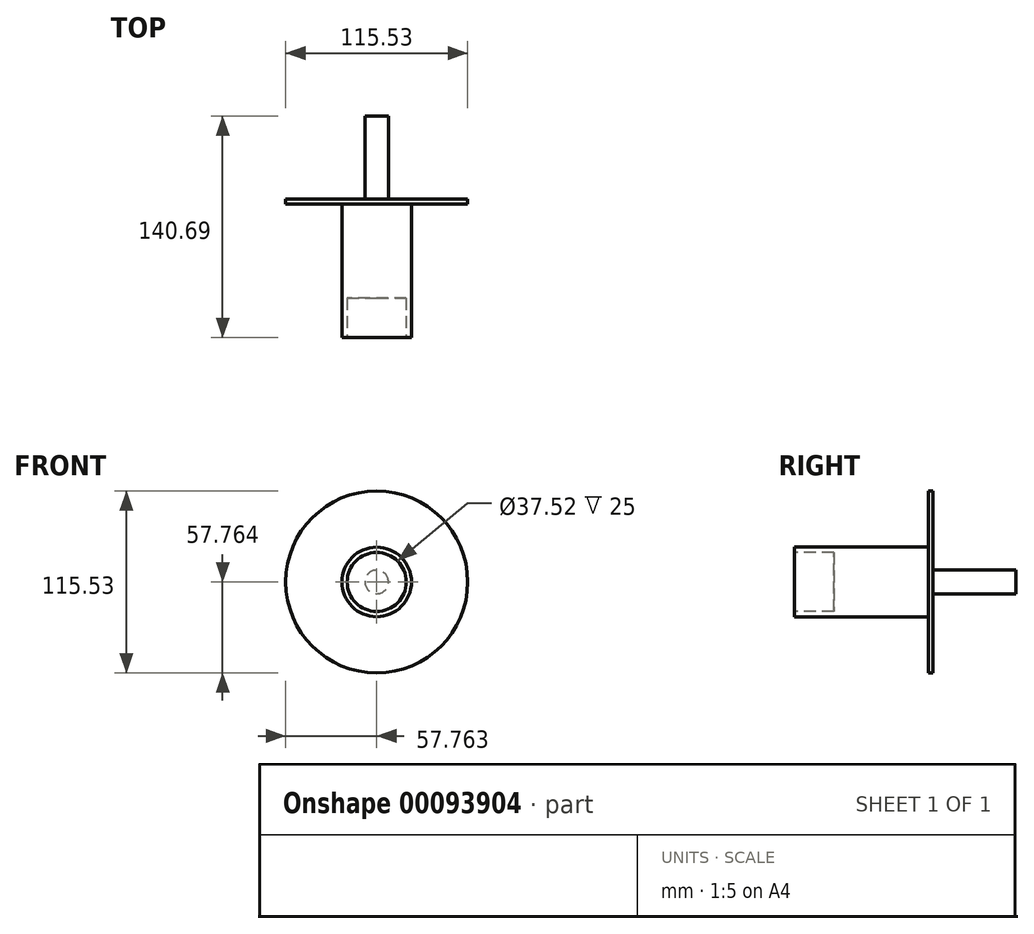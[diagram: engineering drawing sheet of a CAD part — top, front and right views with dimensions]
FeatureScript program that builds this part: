
annotation { "Feature Type Name" : "Feature", "Feature Type Description" : "" }
export const myFeature = defineFeature(function(context is Context, id is Id, definition is map)
    precondition{}
    {
        {
            var Q0;
            Q0=qCreatedBy(makeId("Front.planeOp"),FACE);
            var sketch = newSketch(context, id + "F0", { "sketchPlane" : qUnion([Q0])});
            skCircle(sketch, "E0", {"center": v(-53.8, 33.85) * mm, "radius": 7.5 * mm});
            skSolve(sketch);
        }
        {
            var Q0;
            Q0 = qSketchRegion(id + "F0", true);
            extrude(context, id + "F1", {"entities" : qUnion([Q0]), "depth" : 52.8 * mm});
        }
        {
            var Q0;
            Q0=makeQuery(id+"F1.opExtrude","CAP_FACE",FACE,{"disambiguationData":[OSD([sQuery(id+"F0.wireOp",EDGE,"E0")])],"isStart":false});
            var sketch = newSketch(context, id + "F2", { "sketchPlane" : qUnion([Q0])});
            skCircle(sketch, "E1", {"center": v(-53.8, 33.85) * mm, "radius": 57.77 * mm});
            skSolve(sketch);
        }
        {
            var Q0;
            Q0 = qSketchRegion(id + "F2", true);
            var Q1;
            Q1=makeQuery(id+"F2.imprint","IMPRINT",FACE,{"disambiguationData":[TD([[makeQuery(id+"F2.imprint","IMPRINT",EDGE,{"derivedFrom":sQuery(id+"F2.wireOp",EDGE,"E1")}),1.0]])]});
            extrude(context, id + "F3", {"entities" : qUnion([Q0, Q1]), "operationType" : NewBodyOperationType.ADD, "depth" : 3 * mm});
        }
        {
            var Q0;
            Q0=makeQuery(id+"F3.opExtrude","CAP_FACE",FACE,{"disambiguationData":[OSD([sQuery(id+"F2.wireOp",EDGE,"E1")])],"isStart":false});
            var sketch = newSketch(context, id + "F4", { "sketchPlane" : qUnion([Q0])});
            skCircle(sketch, "E2", {"center": v(-53.8, 33.85) * mm, "radius": 22.1 * mm});
            skSolve(sketch);
        }
        {
            var Q0;
            Q0=makeQuery(id+"F4.imprint","IMPRINT",FACE,{"disambiguationData":[TD([[makeQuery(id+"F4.imprint","IMPRINT",EDGE,{"derivedFrom":sQuery(id+"F4.wireOp",EDGE,"E2")}),1.0]])]});
            extrude(context, id + "F5", {"entities" : qUnion([Q0]), "operationType" : NewBodyOperationType.ADD, "depth" : 84.88 * mm});
        }
        {
            var Q0;
            Q0=makeQuery(id+"F5.opExtrude","CAP_FACE",FACE,{"disambiguationData":[OSD([sQuery(id+"F4.wireOp",EDGE,"E2")])],"isStart":false});
            var sketch = newSketch(context, id + "F6", { "sketchPlane" : qUnion([Q0])});
            skCircle(sketch, "E3", {"center": v(-53.8, 33.85) * mm, "radius": 18.76 * mm});
            skSolve(sketch);
        }
        {
            var Q0;
            Q0 = qSketchRegion(id + "F6", true);
            extrude(context, id + "F7", {"entities" : qUnion([Q0]), "operationType" : NewBodyOperationType.REMOVE, "oppositeDirection" : true, "depth" : 25 * mm});
        }
    });
